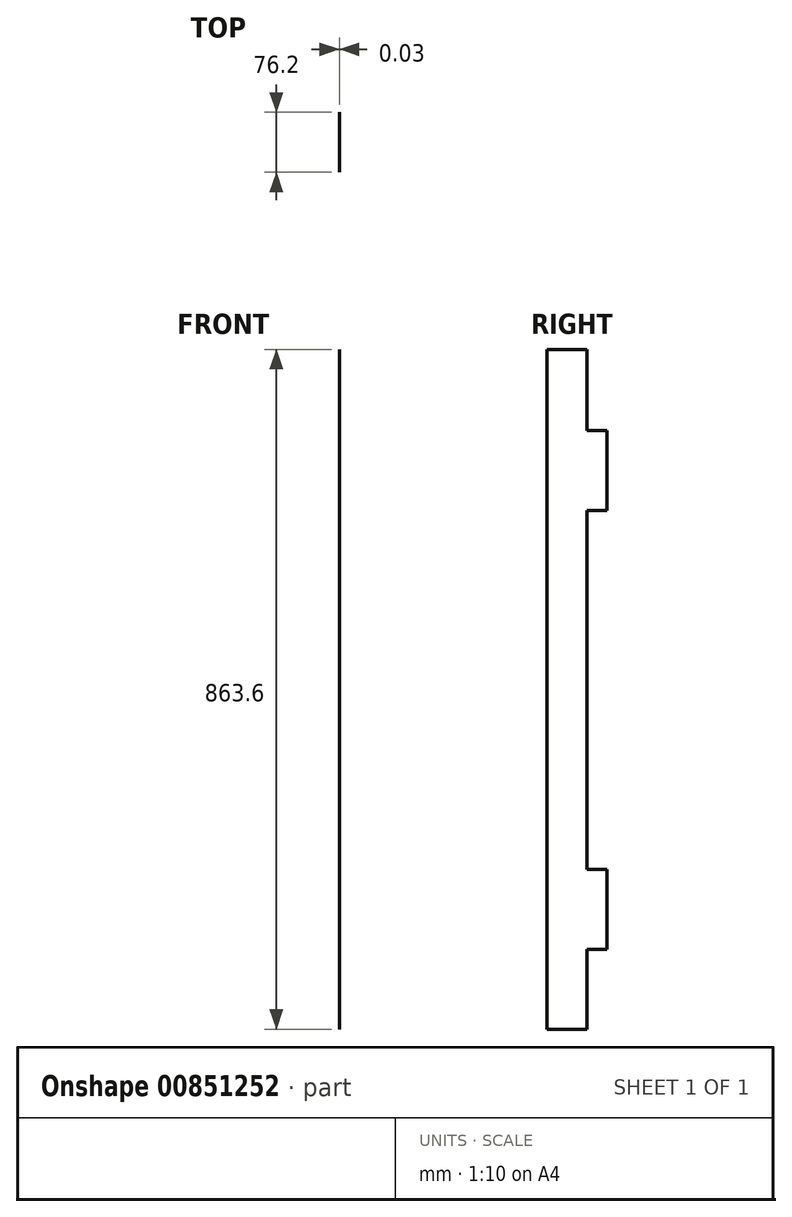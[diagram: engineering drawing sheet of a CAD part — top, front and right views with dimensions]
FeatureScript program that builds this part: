
annotation { "Feature Type Name" : "Feature", "Feature Type Description" : "" }
export const myFeature = defineFeature(function(context is Context, id is Id, definition is map)
    precondition{}
    {
        {
            var Q0;
            Q0=qCreatedBy(makeId("Right.planeOp"),FACE);
            var sketch = newSketch(context, id + "F0", { "sketchPlane" : qUnion([Q0])});
            skLineSegment(sketch, "E0.bottom", {"start": v(-75.36, 447.47) * mm, "end": v(-24.56, 447.47) * mm});
            skLineSegment(sketch, "E0.top", {"start": v(-75.36, -416.13) * mm, "end": v(-24.56, -416.13) * mm});
            skLineSegment(sketch, "E0.left", {"start": v(-75.36, 447.47) * mm, "end": v(-75.36, -416.13) * mm});
            skLineSegment(sketch, "E1", {"start": v(-24.56, 447.47) * mm, "end": v(-24.56, 344.62) * mm});
            skLineSegment(sketch, "E2", {"start": v(-24.56, 344.62) * mm, "end": v(0.84, 344.62) * mm});
            skLineSegment(sketch, "E3", {"start": v(0.84, 344.62) * mm, "end": v(0.84, 243.02) * mm});
            skLineSegment(sketch, "E4", {"start": v(0.84, 243.02) * mm, "end": v(-24.56, 243.02) * mm});
            skLineSegment(sketch, "E5", {"start": v(-24.56, -416.13) * mm, "end": v(-24.56, -314.53) * mm});
            skLineSegment(sketch, "E6", {"start": v(-24.56, -314.53) * mm, "end": v(0.84, -314.53) * mm});
            skLineSegment(sketch, "E7", {"start": v(0.84, -314.53) * mm, "end": v(0.84, -212.93) * mm});
            skLineSegment(sketch, "E8", {"start": v(-24.56, -212.93) * mm, "end": v(0.84, -212.93) * mm});
            skLineSegment(sketch, "E9", {"start": v(-24.56, -212.93) * mm, "end": v(-24.56, 243.02) * mm});
            skSolve(sketch);
        }
        {
            var Q0;
            Q0=makeQuery(id+"F0.imprint","IMPRINT",FACE,{"disambiguationData":[TD([[makeQuery(id+"F0.imprint","IMPRINT",EDGE,{"derivedFrom":sQuery(id+"F0.wireOp",EDGE,"E0.bottom")}),-1.0]])]});
            extrude(context, id + "F1", {"entities" : qUnion([Q0]), "depth" : 3 / 101.6 * mm, "offsetDistance" : 25.4 * mm});
        }
    });
